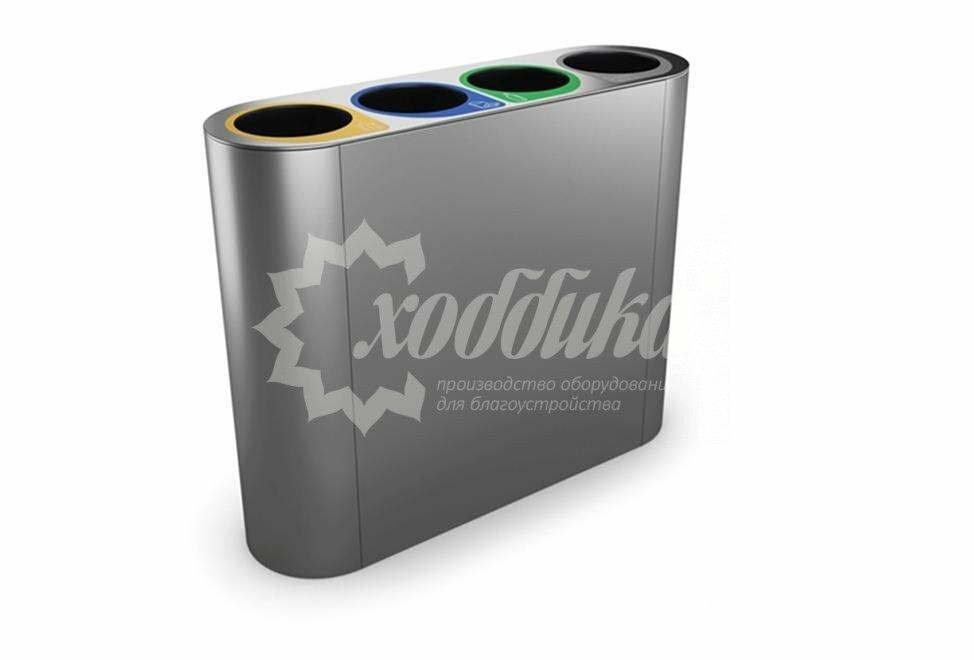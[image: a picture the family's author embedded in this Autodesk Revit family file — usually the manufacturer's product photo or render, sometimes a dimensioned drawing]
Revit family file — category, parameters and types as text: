
# Revit family: Урна для раздельного сбора мусора «Скади» Арт 14042
name_source: partatom
category: Антураж
revit_build: Autodesk Revit 2018 (Build: 20180423_1000(x64)
units: mm (PartAtom-declared; Revit-internal decimal feet)

## family parameters
Всегда вертикально = Да
Источник визуального образа = Геометрия семейства
На основе рабочей плоскости = Нет
Общий = Нет
При загрузке вырезать с полостями = Нет
Точка расчета площади = Нет

## types (2) — shared parameters
URL = https://hobbyka.ru
Артикул товара = Арт. 14042
Высота = 770 мм
Группа модели = Уличные урны
Длина = 1200 мм
Изготовитель = ООО «Хоббика
Изображение типоразмера = Урна для раздельного сбора мусора «Скади» Арт 14042.jpg
Урна №1 = Желтый
Урна №2 = Синий
Урна №3 = Зеленый
Урна №4 = Красный
Ширина = 360 мм

## per-type parameters (varying)
| type | Материал "Нержавеющая сталь" | Материал "Сталь" | Материал изделия | Описание | Цвет урны |
| Урна для раздельного сбора мусора «Скади». Версия Сталь | Нет | Да | Сталь | Урна для раздельного сбора мусора «Скади». Версия: Сталь | Сталь |
| Урна для раздельного сбора мусора «Скади». Версия Нержавеющая сталь | Да | Нет | Нержавеющая сталь | Урна для раздельного сбора мусора «Скади». Версия: Нержавеющая сталь | Нержавеющая сталь |
